# Revit family: IntelliSHOT ePTZ Camera
name_source: partatom
category: Furniture
revit_build: Autodesk Revit 2018 (Build: 20181015_0930(x64)
units: mm (PartAtom-declared; Revit-internal decimal feet)

## family parameters
Always vertical = Yes
Cut with Voids When Loaded = No
Room Calculation Point = No
Shared = Yes
Work Plane-Based = Yes

## types (2) — shared parameters
Aperture/detail = 16 steps
Aspect ratio = IP (H.264) Streaming: 16:9, 3:2 and 4:3 | HDMI: 16:9 | USB: 16:9
Audio Processing (Internal Mics) = Acoustic Echo Cancellation
Backlight compensation = On/off
Cardioid Type = Omnidirectional
Default Elevation = 48 "
Depth = 4.5” (11.43 cm)
Enhanced Wide Dynamic Range = Yes
Focusing system = Auto Focus / Manual Focus Mode / One-push Trigger Mode
Frequency Response = Flat
Gain = Auto / Manual (0 to 33 dB)
Image device = 1/2.5-Type Exmor R CMOS sensor
Invertible = Yes
Lens and Horizontal FOV = 30x zoom, 20x optical zoom + 10x IntelliZoom, 70.2° (Wide End) 3.1° (Tele End)
Manual Tilt Range = -20°, +30°
Microphone Configuration = 2x Beamforming
Min. working distance = 80mm (wide), 800mm (tele)
Min.illumination = 1.6 lux; 100+ lux recommended
Noise Reduction = Yes
Outputs/protocols = IP (H.264), USB 3.0, HDMI 1.4, Balanced Audio
Pixels = 8.51 million; (8.57M Total Megapixels)
Power = PoE+
Presets = 16 + Custom Home
Remote management = Wireless Remote, web interface via Vaddio Device Controller, Telnet
Resolutions/frame rates = Up to 1080p/30
S/N ratio = More than 50 dB
Signal to Noise Ratio = 64.3dB
Spotlight Compensation Mode = Yes
Warranty = 3 years with 1 year Advanced Replacement
Weight = 4.25 lbs (1.93 kg)
White balance = Auto, ATW, Indoor, Outdoor, One-push, Manual
Width = 6” (15.24 cm)

## per-type parameters (varying)
| type | Height | Legrand_Finish | Operating/storage humidity (relative) | Operating/storage temperature |
| IntelliSHOT ePTZ Camera_Black | 8.375” (21.27 cm) | Legrand_Black | 20% to 80% RH, non-condensing | 0°C to +40°C (32°F to 104°F) |
| IntelliSHOT ePTZ Camera_White | 4.25 lbs (1.93 kg) | Legrand_White | 0°C to +40°C (32°F to 104°F) | 20% to 80% RH, non-condensing |

## geometry (parser evidence)
native form markers: Sweep x5
no freeform markers — native parametric forms only
